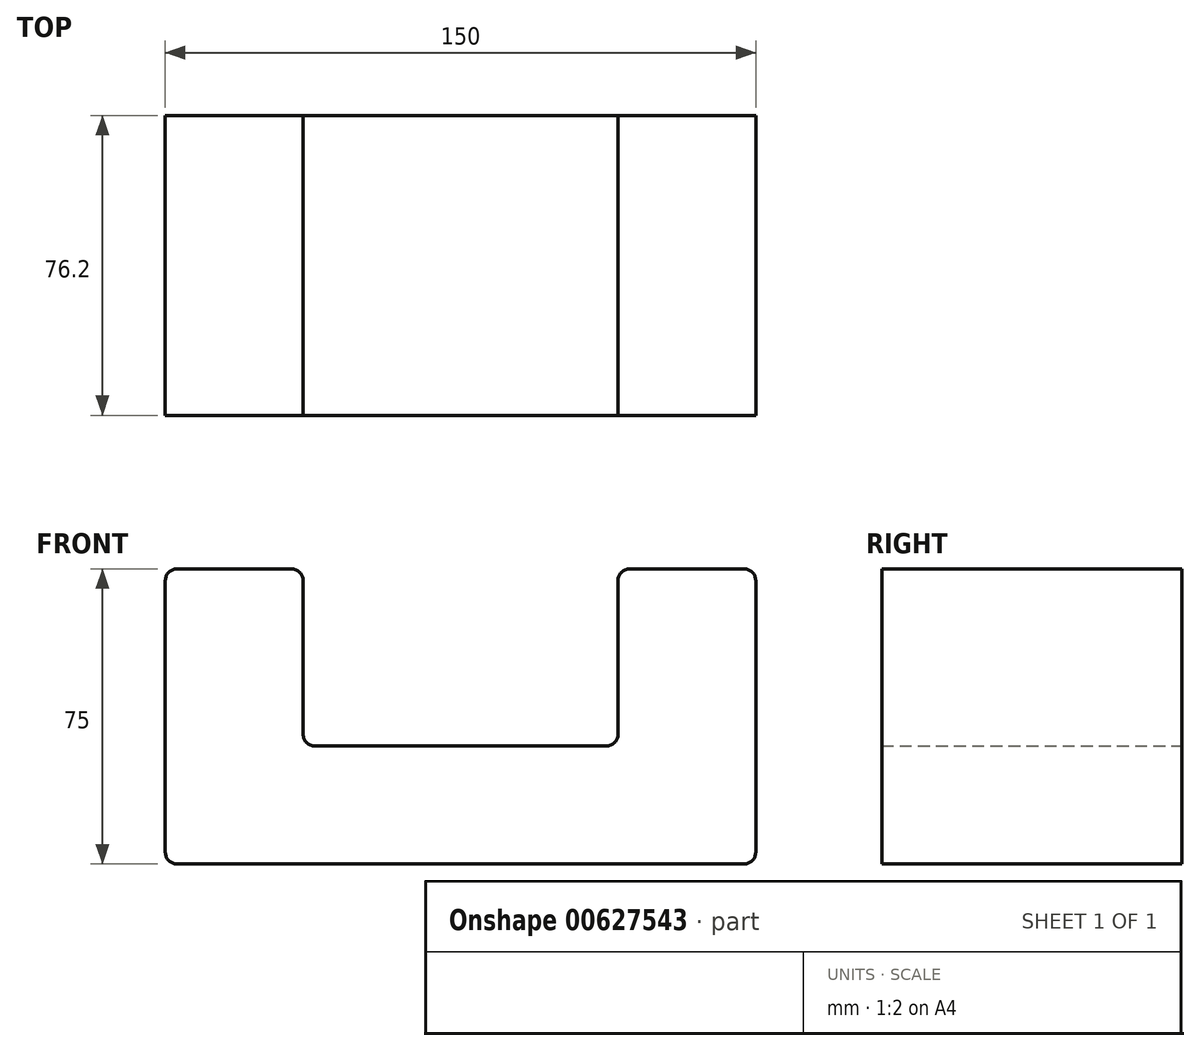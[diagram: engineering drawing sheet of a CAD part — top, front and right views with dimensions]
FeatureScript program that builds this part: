
annotation { "Feature Type Name" : "Feature", "Feature Type Description" : "" }
export const myFeature = defineFeature(function(context is Context, id is Id, definition is map)
    precondition{}
    {
        {
            var Q0;
            Q0=qCreatedBy(makeId("Front.planeOp"),FACE);
            var sketch = newSketch(context, id + "F0", { "sketchPlane" : qUnion([Q0])});
            skLineSegment(sketch, "E0.bottom", {"start": v(-72, -37.5) * mm, "end": v(72, -37.5) * mm});
            skLineSegment(sketch, "E0.top", {"start": v(-72, 37.5) * mm, "end": v(-43, 37.5) * mm});
            skLineSegment(sketch, "E0.left", {"start": v(-75, -34.5) * mm, "end": v(-75, 34.5) * mm});
            skLineSegment(sketch, "E0.right", {"start": v(75, -34.5) * mm, "end": v(75, 34.5) * mm});
            skPoint(sketch, "E0.middle", {"position": v(0, 0) * mm});
            skPoint(sketch, "E1.visualSharp", {"position": v(-75, 37.5) * mm});
            skArc(sketch, "E1.filletArc", {"start": v(-72, 37.5) * mm, "mid": v(-74.12, 36.62) * mm, "end": v(-75, 34.5) * mm});
            skPoint(sketch, "E2.visualSharp", {"position": v(75, 37.5) * mm});
            skArc(sketch, "E2.filletArc", {"start": v(75, 34.5) * mm, "mid": v(74.12, 36.62) * mm, "end": v(72, 37.5) * mm});
            skPoint(sketch, "E3.visualSharp", {"position": v(75, -37.5) * mm});
            skArc(sketch, "E3.filletArc", {"start": v(72, -37.5) * mm, "mid": v(74.12, -36.62) * mm, "end": v(75, -34.5) * mm});
            skPoint(sketch, "E4.visualSharp", {"position": v(-75, -37.5) * mm});
            skArc(sketch, "E4.filletArc", {"start": v(-75, -34.5) * mm, "mid": v(-74.12, -36.62) * mm, "end": v(-72, -37.5) * mm});
            skLineSegment(sketch, "E5", {"start": v(-40, 34.5) * mm, "end": v(-40, -4.5) * mm});
            skLineSegment(sketch, "E6", {"start": v(-37, -7.5) * mm, "end": v(37, -7.5) * mm});
            skLineSegment(sketch, "E7", {"start": v(40, -4.5) * mm, "end": v(40, 34.5) * mm});
            skLineSegment(sketch, "E8.trimOffspring", {"start": v(43, 37.5) * mm, "end": v(72, 37.5) * mm});
            skPoint(sketch, "E9.visualSharp", {"position": v(40, 37.5) * mm});
            skArc(sketch, "E9.filletArc", {"start": v(43, 37.5) * mm, "mid": v(40.88, 36.62) * mm, "end": v(40, 34.5) * mm});
            skPoint(sketch, "E10.visualSharp", {"position": v(40, -7.5) * mm});
            skArc(sketch, "E10.filletArc", {"start": v(37, -7.5) * mm, "mid": v(39.12, -6.62) * mm, "end": v(40, -4.5) * mm});
            skPoint(sketch, "E11.visualSharp", {"position": v(-40, -7.5) * mm});
            skArc(sketch, "E11.filletArc", {"start": v(-40, -4.5) * mm, "mid": v(-39.12, -6.62) * mm, "end": v(-37, -7.5) * mm});
            skPoint(sketch, "E12.visualSharp", {"position": v(-40, 37.5) * mm});
            skArc(sketch, "E12.filletArc", {"start": v(-40, 34.5) * mm, "mid": v(-40.88, 36.62) * mm, "end": v(-43, 37.5) * mm});
            skSolve(sketch);
        }
        {
            var Q0;
            Q0=makeQuery(id+"F0.imprint","IMPRINT",FACE,{"disambiguationData":[TD([[makeQuery(id+"F0.imprint","IMPRINT",EDGE,{"derivedFrom":sQuery(id+"F0.wireOp",EDGE,"E0.bottom")}),1.0]])]});
            extrude(context, id + "F1", {"entities" : qUnion([Q0]), "depth" : 76.2 * mm, "offsetDistance" : 25.4 * mm});
        }
    });
